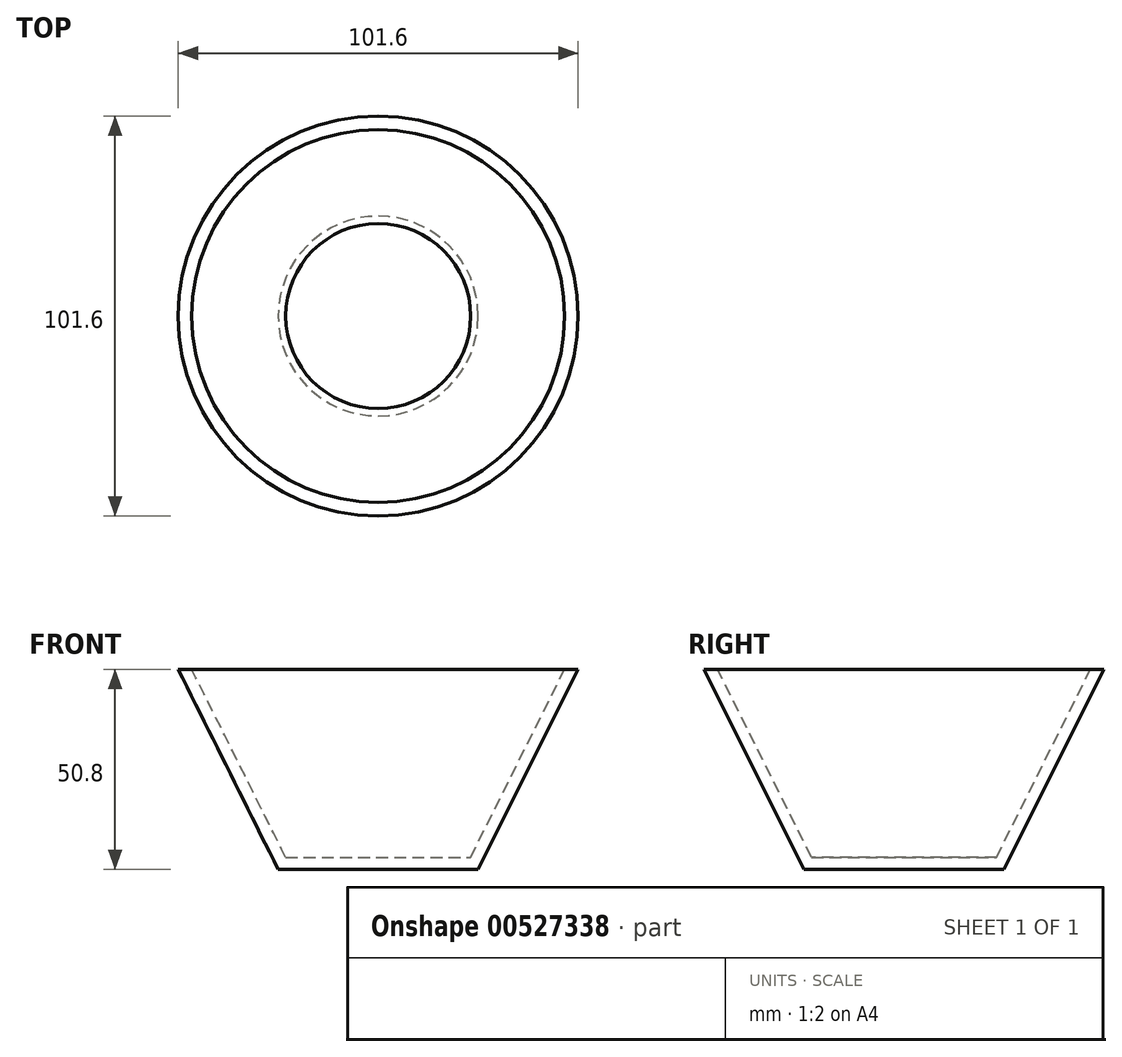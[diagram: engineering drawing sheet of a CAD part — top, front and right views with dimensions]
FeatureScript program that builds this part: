
annotation { "Feature Type Name" : "Feature", "Feature Type Description" : "" }
export const myFeature = defineFeature(function(context is Context, id is Id, definition is map)
    precondition{}
    {
        {
            var Q0;
            Q0=qCreatedBy(makeId("Front.planeOp"),FACE);
            var sketch = newSketch(context, id + "F0", { "sketchPlane" : qUnion([Q0])});
            skLineSegment(sketch, "E0", {"start": v(0, 0) * mm, "end": v(0, 50.8) * mm, "construction": true});
            skLineSegment(sketch, "E1", {"start": v(0, 0) * mm, "end": v(25.4, 0) * mm});
            skLineSegment(sketch, "E2", {"start": v(25.4, 0) * mm, "end": v(50.8, 50.8) * mm});
            skLineSegment(sketch, "E3.0", {"start": v(23.5, 3.07) * mm, "end": v(47.36, 50.8) * mm});
            skLineSegment(sketch, "E3.1", {"start": v(0, 3.07) * mm, "end": v(23.5, 3.07) * mm});
            skLineSegment(sketch, "E4", {"start": v(0, 3.07) * mm, "end": v(0, 0) * mm});
            skLineSegment(sketch, "E5", {"start": v(47.36, 50.8) * mm, "end": v(50.8, 50.8) * mm});
            skSolve(sketch);
        }
        {
            var Q0;
            Q0=makeQuery(id+"F0.imprint","IMPRINT",FACE,{"disambiguationData":[TD([[makeQuery(id+"F0.imprint","IMPRINT",EDGE,{"derivedFrom":sQuery(id+"F0.wireOp",EDGE,"E1")}),1.0]])]});
            var Q1;
            Q1=sQuery(id+"F0.wireOp",EDGE,"E0");
            revolve(context, id + "F1", {"entities" : qUnion([Q0]), "axis" : qUnion([Q1]), "revolveType" : RevolveType.FULL});
        }
    });
